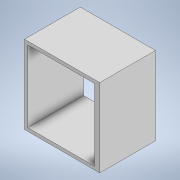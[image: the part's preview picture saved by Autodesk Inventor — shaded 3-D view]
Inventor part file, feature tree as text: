
AUTODESK INVENTOR PART (.ipt)
format: ipt  version: 2020.3 (Build 243373000, 373)  size: 146,944 bytes
history: native  units: mm
features: extrude x6, sketch x6, projected_geometry x3
ambient origin geometry x8: Origin, YZ Plane, XZ Plane, XY Plane, X Axis, Y Axis, Z Axis, Center Point
bodies: Solid1 (feature_tree)
feature tree (15):
  extrude  "Extrusion1"  Depth=109.349mm
  extrude  "Extrusion5"  Depth=5.0mm TaperAngle=0.0deg
  extrude  "Extrusion6"  Depth=119.349mm
  extrude  "Extrusion7"  Depth=59.6745mm
  extrude  "Extrusion8"  Depth=2.778mm TaperAngle=0.0deg
  extrude  "Extrusion9"  Depth=3.0mm TaperAngle=0.0deg
  sketch  "Sketch1"  dims[d0=101.968mm d1=109.349mm]
  sketch  "Sketch5"  dims[d2=5.0mm d3=50.0mm d4=0.0mm]
  sketch  "Sketch6"  dims[d14=119.349mm d15=19.05mm]
  projected_geometry  "Projected Loop4"
  sketch  "Sketch7"  dims[d16=25.0mm d17=59.6745mm]
  sketch  "Sketch8"  dims[d18=2.778mm d19=0.0mm d20=2.778mm d21=0.0mm]
  projected_geometry  "Projected Loop5"
  sketch  "Sketch9"  dims[d22=14.99mm d23=3.0mm d24=0.0mm d25=17.5mm d26=0.0mm d27=17.5mm d28=0.0mm]
  projected_geometry  "Projected Loop6"
